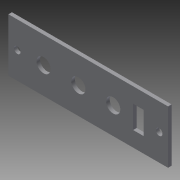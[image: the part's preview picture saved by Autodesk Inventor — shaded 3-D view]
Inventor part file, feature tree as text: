
AUTODESK INVENTOR PART (.ipt)
format: ipt  version: 2014 SP1 (Build 180222100, 222)  size: 116,224 bytes
history: native  units: in
note: dims shown in document units (in); Inventor stores cm internally (conversion verified against a paired STEP export)
features: extrude x3, sketch x3
ambient origin geometry x8: Origin, YZ Plane, XZ Plane, XY Plane, X Axis, Y Axis, Z Axis, Center Point
bodies: Solid1 (feature_tree)
feature tree (6):
  extrude  "Extrusion1"  Depth=0.05in
  extrude  "Extrusion2"  Depth=0.7487in
  extrude  "Extrusion3"  Depth=0.05in
  sketch  "Sketch1"  dims[d0=0.05in d1=0.0in d2=0.2in]
  sketch  "Sketch2"  dims[d3=2.25in d4=0.7487in]
  sketch  "Sketch3"  dims[d5=0.125in d6=0.125in d7=0.22in d8=0.39in d9=0.18in d10=0.307in d11=0.491in d12=0.491in d13=0.2in d14=0.2in d16=0.15in d17=0.1in d18=0.0in d19=0.05in d20=0.0in]
